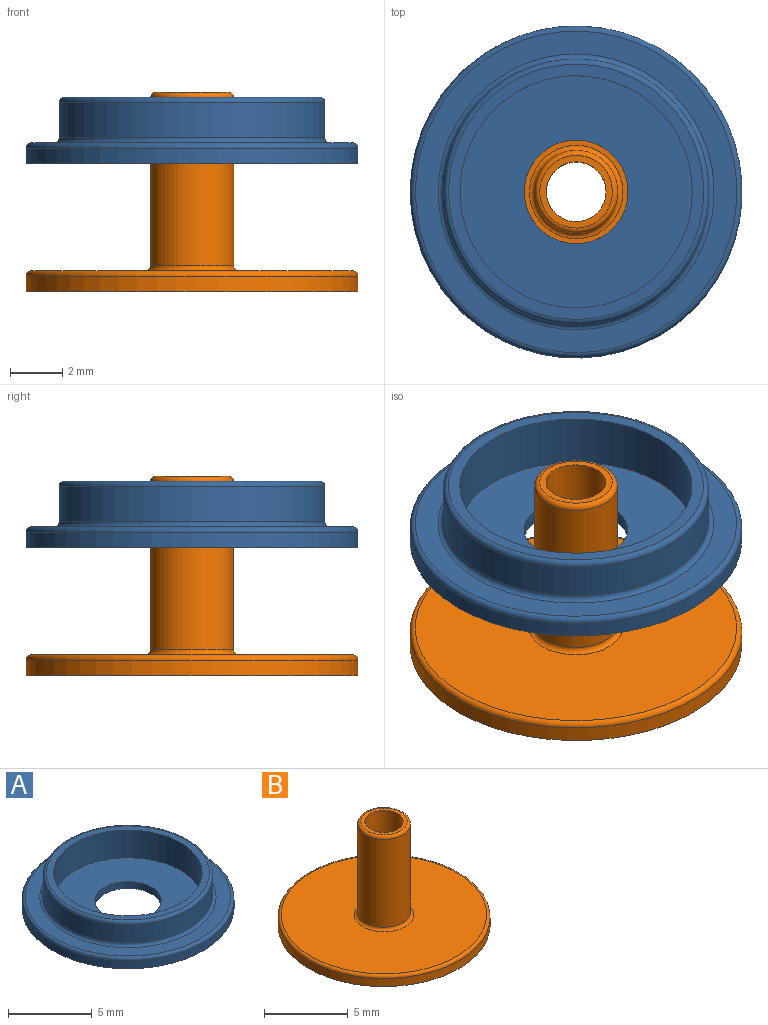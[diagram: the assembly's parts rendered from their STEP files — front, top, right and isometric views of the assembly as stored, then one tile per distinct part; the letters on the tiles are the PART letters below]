
ASSEMBLY  parts=2 mates=2
PART A: 11 faces, bbox 13.7x13.7x2.5 mm
  f0: cylinder r=1.98mm len=3.97mm, axis (0,0,-1), area 6.3mm2, adj f5,f10
  f1: torus R=5.28mm, axis (0,0,-1), area 10.1mm2, adj f2,f8
  f2: cylinder r=5.08mm len=10.16mm, axis (0,0,-1), area 43.1mm2, adj f1,f3
  f3: torus R=4.88mm, axis (0,0,-1), area 9.8mm2, adj f2,f4
  f4: plane 9.76x9.76mm, normal (0,0,1), area 12.8mm2, adj f3,f9
  f5: plane 12.7x12.7mm, normal (0,0,-1), area 114.3mm2, adj f0,f6
  f6: cylinder r=6.35mm len=12.7mm, axis (0,0,-1), area 23.8mm2, adj f5,f7
  f7: torus R=6.15mm, axis (0,0,-1), area 12.3mm2, adj f6,f8
  f8: plane 12.3x12.3mm, normal (0,0,1), area 31.4mm2, adj f1,f7
  f9: cylinder r=4.45mm len=8.89mm, axis (0,0,1), area 56.8mm2, adj f4,f10
  f10: plane 8.89x8.89mm, normal (0,0,1), area 49.7mm2, adj f0,f9
PART B: 9 faces, bbox 13.7x13.7x7.6 mm
  f0: cylinder r=6.35mm len=12.7mm, axis (0,0,-1), area 23.8mm2, adj f1,f7
  f1: torus R=6.15mm, axis (0,0,-1), area 12.3mm2, adj f0,f2
  f2: plane 12.3x12.3mm, normal (0,0,1), area 108.9mm2, adj f1,f3
  f3: torus R=1.79mm, axis (0,0,-1), area 3.3mm2, adj f2,f4
  f4: cylinder r=1.59mm len=6.43mm, axis (0,0,-1), area 64.1mm2, adj f3,f5
  f5: torus R=1.39mm, axis (0,0,-1), area 3mm2, adj f4,f6
  f6: plane 2.78x2.78mm, normal (0,0,1), area 2mm2, adj f5,f8
  f7: plane 12.7x12.7mm, normal (0,0,-1), area 122.6mm2, adj f0,f8
  f8: cylinder r=1.14mm len=7.62mm, axis (0,0,1), area 54.7mm2, adj f6,f7
PLACE A t=(0,0,4.89)mm
PLACE B at identity fixed
MATE slider A.f0 <-> B.f0  axis (0,0,-1) through (0,0,5.4)mm
MATE fastened A.f0 <-> B.f0  axis (0,0,-1) through (0,0,4.89)mm
